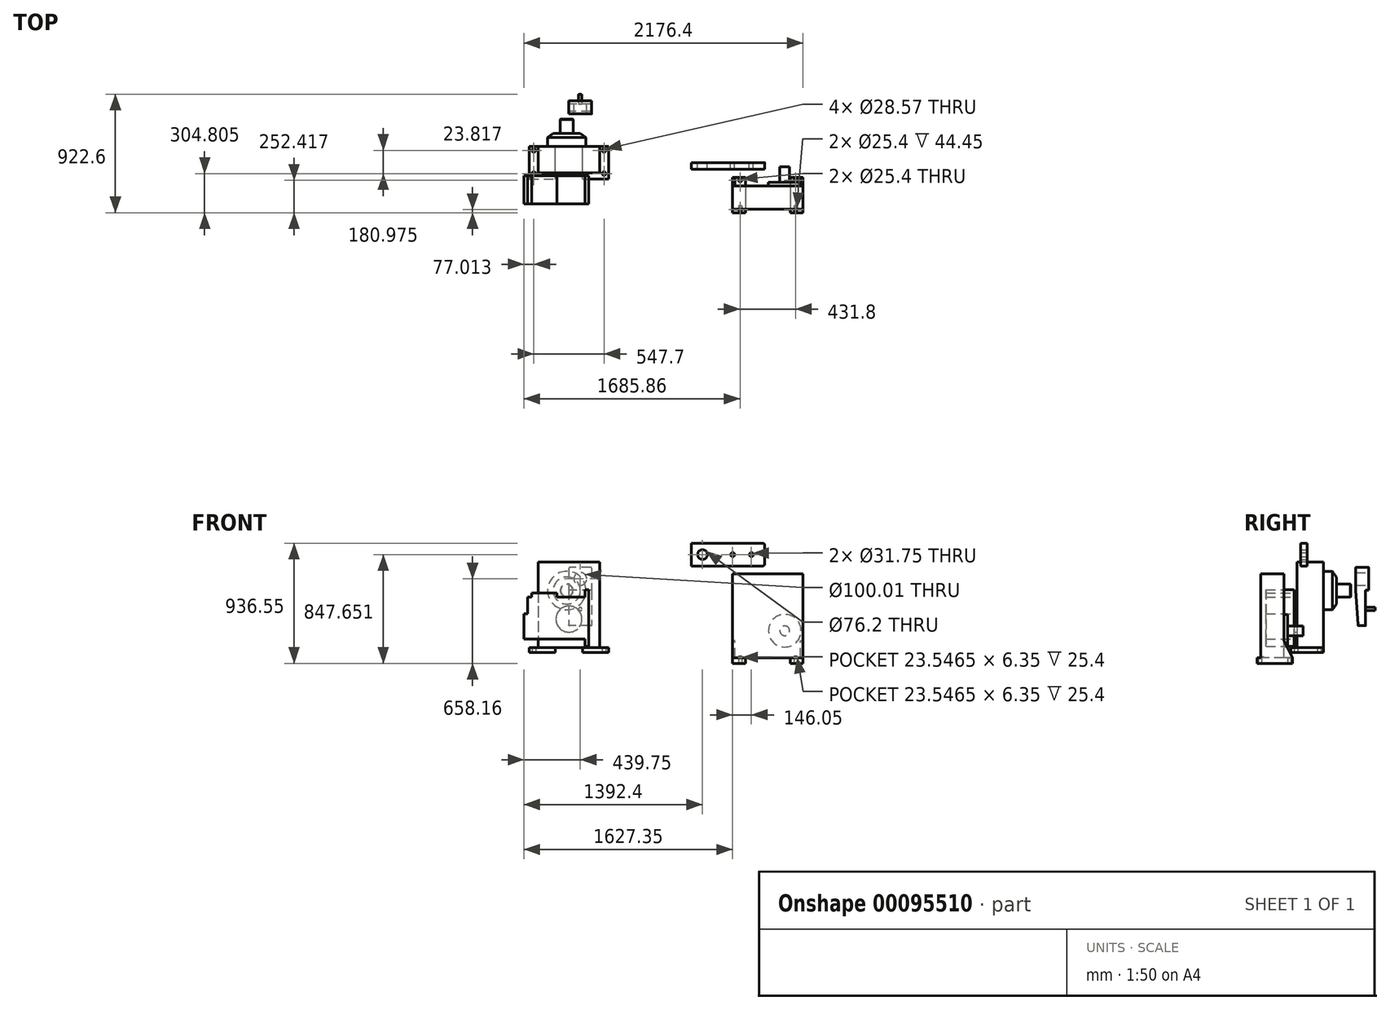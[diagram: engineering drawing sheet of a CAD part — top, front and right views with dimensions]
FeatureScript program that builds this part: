
annotation { "Feature Type Name" : "Feature", "Feature Type Description" : "" }
export const myFeature = defineFeature(function(context is Context, id is Id, definition is map)
    precondition{}
    {
        {
            var Q0;
            Q0=qCreatedBy(makeId("Top.planeOp"),FACE);
            var sketch = newSketch(context, id + "F0", { "sketchPlane" : qUnion([Q0])});
            skLineSegment(sketch, "E0.bottom", {"start": v(-310.36, 127) * mm, "end": v(310.36, 127) * mm});
            skLineSegment(sketch, "E0.top", {"start": v(-310.36, -127) * mm, "end": v(310.36, -127) * mm});
            skLineSegment(sketch, "E0.left", {"start": v(-310.36, 127) * mm, "end": v(-310.36, -127) * mm});
            skLineSegment(sketch, "E0.right", {"start": v(310.36, 127) * mm, "end": v(310.36, -127) * mm});
            skPoint(sketch, "E0.middle", {"position": v(0, 0) * mm});
            skCircle(sketch, "E1", {"center": v(-273.84, -85.73) * mm, "radius": 14.29 * mm});
            skCircle(sketch, "E2.1.0.0", {"center": v(273.86, -85.73) * mm, "radius": 14.29 * mm});
            skLineSegment(sketch, "E2.direction1", {"start": v(-273.84, -85.73) * mm, "end": v(273.86, -85.73) * mm, "construction": true});
            skCircle(sketch, "E3.0.1.0", {"center": v(-273.84, 95.25) * mm, "radius": 14.29 * mm});
            skCircle(sketch, "E3.0.1.1", {"center": v(273.86, 95.25) * mm, "radius": 14.29 * mm});
            skLineSegment(sketch, "E3.direction1", {"start": v(-273.84, -85.73) * mm, "end": v(-248.44, -85.73) * mm, "construction": true});
            skLineSegment(sketch, "E3.direction2", {"start": v(-273.84, -85.73) * mm, "end": v(-273.84, 95.25) * mm, "construction": true});
            skSolve(sketch);
        }
        {
            var Q0;
            Q0=makeQuery(id+"F0.imprint","IMPRINT",FACE,{"disambiguationData":[TD([[makeQuery(id+"F0.imprint","IMPRINT",EDGE,{"derivedFrom":sQuery(id+"F0.wireOp",EDGE,"E0.bottom")}),-1.0]])]});
            extrude(context, id + "F1", {"entities" : qUnion([Q0]), "depth" : 39.7 * mm});
        }
        {
            var Q0;
            Q0=makeQuery(id+"F1.opExtrude","CAP_FACE",FACE,{"disambiguationData":[OSD([sQuery(id+"F0.wireOp",EDGE,"E0.bottom"),sQuery(id+"F0.wireOp",EDGE,"E0.top"),sQuery(id+"F0.wireOp",EDGE,"E0.left"),sQuery(id+"F0.wireOp",EDGE,"E0.right"),sQuery(id+"F0.wireOp",EDGE,"E1"),sQuery(id+"F0.wireOp",EDGE,"E2.1.0.0"),sQuery(id+"F0.wireOp",EDGE,"E3.0.1.0"),sQuery(id+"F0.wireOp",EDGE,"E3.0.1.1")])],"isStart":false});
            var sketch = newSketch(context, id + "F2", { "sketchPlane" : qUnion([Q0])});
            skLineSegment(sketch, "E4.bottom", {"start": v(-240.51, 127) * mm, "end": v(240.51, 127) * mm});
            skLineSegment(sketch, "E4.top", {"start": v(-240.51, -79.37) * mm, "end": v(240.51, -79.37) * mm});
            skLineSegment(sketch, "E4.left", {"start": v(-240.51, 127) * mm, "end": v(-240.51, -79.37) * mm});
            skLineSegment(sketch, "E4.right", {"start": v(240.51, 127) * mm, "end": v(240.51, -79.37) * mm});
            skSolve(sketch);
        }
        {
            var Q0;
            Q0=makeQuery(id+"F2.imprint","IMPRINT",FACE,{"disambiguationData":[TD([[makeQuery(id+"F2.imprint","IMPRINT",EDGE,{"derivedFrom":sQuery(id+"F2.wireOp",EDGE,"E4.bottom")}),-1.0]])]});
            extrude(context, id + "F3", {"entities" : qUnion([Q0]), "operationType" : NewBodyOperationType.ADD, "depth" : 666.75 * mm});
        }
        {
            var Q0;
            Q0=makeQuery(id+"F3.boolean.opBoolean","MERGE",FACE,{"derivedFrom":[makeQuery(id+"F1.opExtrude","SWEPT_FACE",FACE,{"disambiguationData":[OSD([sQuery(id+"F0.wireOp",EDGE,"E0.bottom")])]}),makeQuery(id+"F3.opExtrude","SWEPT_FACE",FACE,{"disambiguationData":[OSD([sQuery(id+"F2.wireOp",EDGE,"E4.bottom")])]})]});
            var sketch = newSketch(context, id + "F4", { "sketchPlane" : qUnion([Q0])});
            skCircle(sketch, "E5", {"center": v(16.66, 483.4) * mm, "radius": 150.02 * mm});
            skSolve(sketch);
        }
        {
            var Q0;
            Q0=makeQuery(id+"F4.imprint","IMPRINT",FACE,{"disambiguationData":[TD([[makeQuery(id+"F4.imprint","IMPRINT",EDGE,{"derivedFrom":sQuery(id+"F4.wireOp",EDGE,"E5")}),1.0]])]});
            extrude(context, id + "F5", {"entities" : qUnion([Q0]), "operationType" : NewBodyOperationType.ADD, "depth" : 101.6 * mm});
        }
        {
            var Q0;
            Q0=makeQuery(id+"F5.opExtrude","CAP_FACE",FACE,{"disambiguationData":[OSD([sQuery(id+"F4.wireOp",EDGE,"E5")])],"isStart":false});
            chamfer(context, id + "F6", {"entities" : qUnion([Q0]), "chamferType" : ChamferType.TWO_OFFSETS, "width1" : 31.75 * mm, "oppositeDirection" : false, "width2" : 44.45 * mm, "tangentPropagation" : true});
        }
        {
            var Q0;
            Q0=qCreatedBy(makeId("Right.planeOp"),FACE);
            var sketch = newSketch(context, id + "F7", { "sketchPlane" : qUnion([Q0])});
            skLineSegment(sketch, "E6.bottom", {"start": v(379.67, 663.04) * mm, "end": v(481.27, 663.04) * mm});
            skLineSegment(sketch, "E7", {"start": v(379.67, 485.24) * mm, "end": v(481.27, 485.24) * mm});
            skLineSegment(sketch, "E8", {"start": v(455.87, 485.24) * mm, "end": v(455.87, 209.02) * mm});
            skLineSegment(sketch, "E9", {"start": v(379.67, 485.24) * mm, "end": v(398.72, 209.02) * mm});
            skLineSegment(sketch, "E10", {"start": v(379.67, 663.04) * mm, "end": v(379.67, 485.24) * mm});
            skLineSegment(sketch, "E11", {"start": v(481.27, 663.04) * mm, "end": v(481.27, 485.24) * mm});
            skLineSegment(sketch, "E12", {"start": v(398.72, 209.02) * mm, "end": v(455.87, 209.02) * mm});
            skSolve(sketch);
        }
        {
            var Q0;
            Q0=makeQuery(id+"F7.imprint","IMPRINT",FACE,{"disambiguationData":[TD([[makeQuery(id+"F7.imprint","IMPRINT",EDGE,{"derivedFrom":sQuery(id+"F7.wireOp",EDGE,"E6.bottom")}),-1.0]])]});
            var Q1;
            {var subQ2=sQuery(id+"F7.wireOp",EDGE,"E8");Q1=makeQuery(id+"F7.imprint","IMPRINT",FACE,{"disambiguationData":[TD([[makeQuery(id+"F7.imprint","IMPRINT",EDGE,{"derivedFrom":subQ2}),-1.0]])]});}
            extrude(context, id + "F8", {"entities" : qUnion([Q0, Q1]), "depth" : 177.8 * mm});
        }
        {
            var Q0;
            Q0=makeQuery(id+"F8.opExtrude","SWEPT_FACE",FACE,{"disambiguationData":[OSD([sQuery(id+"F7.wireOp",EDGE,"E11")])]});
            var sketch = newSketch(context, id + "F9", { "sketchPlane" : qUnion([Q0])});
            skLineSegment(sketch, "E13", {"start": v(-177.8, 485.24) * mm, "end": v(-177.8, 656.7) * mm});
            skLineSegment(sketch, "E14", {"start": v(-171.45, 663.04) * mm, "end": v(0, 663.04) * mm});
            skPoint(sketch, "E15.visualSharp", {"position": v(-177.8, 663.04) * mm});
            skArc(sketch, "E15.filletArc", {"start": v(-171.45, 663.04) * mm, "mid": v(-175.94, 661.18) * mm, "end": v(-177.8, 656.7) * mm});
            skSolve(sketch);
        }
        {
            var Q0;
            {var subQ0=sQuery(id+"F9.wireOp",EDGE,"E15.filletArc");Q0=makeQuery(id+"F9.imprint","IMPRINT",FACE,{"disambiguationData":[TD([[makeQuery(id+"F9.imprint","IMPRINT",EDGE,{"derivedFrom":subQ0}),-1.0]])]});}
            extrude(context, id + "F10", {"entities" : qUnion([Q0]), "operationType" : NewBodyOperationType.REMOVE, "endBound" : BoundingType.UP_TO_NEXT, "oppositeDirection" : true, "depth" : 25.4 * mm});
        }
        {
            var Q0;
            Q0=makeQuery(id+"F8.opExtrude","SWEPT_FACE",FACE,{"disambiguationData":[OSD([sQuery(id+"F7.wireOp",EDGE,"E11")])]});
            var sketch = newSketch(context, id + "F11", { "sketchPlane" : qUnion([Q0])});
            skLineSegment(sketch, "E16", {"start": v(-39.2, 663.04) * mm, "end": v(-6.35, 663.04) * mm});
            skLineSegment(sketch, "E17", {"start": v(0, 656.7) * mm, "end": v(0, 648.47) * mm});
            skPoint(sketch, "E18.visualSharp", {"position": v(0, 663.04) * mm});
            skArc(sketch, "E18.filletArc", {"start": v(0, 656.7) * mm, "mid": v(-1.86, 661.18) * mm, "end": v(-6.35, 663.04) * mm});
            skSolve(sketch);
        }
        {
            var Q0;
            {var subQ0=sQuery(id+"F11.wireOp",EDGE,"E18.filletArc");Q0=makeQuery(id+"F11.imprint","IMPRINT",FACE,{"disambiguationData":[TD([[makeQuery(id+"F11.imprint","IMPRINT",EDGE,{"derivedFrom":subQ0}),-1.0]])]});}
            extrude(context, id + "F12", {"entities" : qUnion([Q0]), "operationType" : NewBodyOperationType.REMOVE, "endBound" : BoundingType.UP_TO_NEXT, "oppositeDirection" : true, "depth" : 25.4 * mm});
        }
        {
            var Q0;
            Q0=makeQuery(id+"F8.opExtrude","SWEPT_FACE",FACE,{"disambiguationData":[OSD([sQuery(id+"F7.wireOp",EDGE,"E8")])]});
            var sketch = newSketch(context, id + "F13", { "sketchPlane" : qUnion([Q0])});
            skLineSegment(sketch, "E19", {"start": v(-177.8, 248.8) * mm, "end": v(-177.8, 215.37) * mm});
            skLineSegment(sketch, "E20", {"start": v(-171.45, 209.02) * mm, "end": v(-6.35, 209.02) * mm});
            skLineSegment(sketch, "E21", {"start": v(0, 215.37) * mm, "end": v(0, 249.23) * mm});
            skPoint(sketch, "E22.visualSharp", {"position": v(-177.8, 209.02) * mm});
            skArc(sketch, "E22.filletArc", {"start": v(-177.8, 215.37) * mm, "mid": v(-175.94, 210.88) * mm, "end": v(-171.45, 209.02) * mm});
            skPoint(sketch, "E23.visualSharp", {"position": v(0, 209.02) * mm});
            skArc(sketch, "E23.filletArc", {"start": v(-6.35, 209.02) * mm, "mid": v(-1.86, 210.88) * mm, "end": v(0, 215.37) * mm});
            skSolve(sketch);
        }
        {
            var Q0;
            {var subQ0=sQuery(id+"F13.wireOp",EDGE,"E22.filletArc");Q0=makeQuery(id+"F13.imprint","IMPRINT",FACE,{"disambiguationData":[TD([[makeQuery(id+"F13.imprint","IMPRINT",EDGE,{"derivedFrom":subQ0}),-1.0]])]});}
            extrude(context, id + "F14", {"entities" : qUnion([Q0]), "operationType" : NewBodyOperationType.REMOVE, "endBound" : BoundingType.UP_TO_NEXT, "oppositeDirection" : true, "depth" : 25.4 * mm});
        }
        {
            var Q0;
            {var subQ0=sQuery(id+"F13.wireOp",EDGE,"E23.filletArc");Q0=makeQuery(id+"F13.imprint","IMPRINT",FACE,{"disambiguationData":[TD([[makeQuery(id+"F13.imprint","IMPRINT",EDGE,{"derivedFrom":subQ0}),-1.0]])]});}
            extrude(context, id + "F15", {"entities" : qUnion([Q0]), "operationType" : NewBodyOperationType.REMOVE, "endBound" : BoundingType.UP_TO_NEXT, "oppositeDirection" : true, "depth" : 25.4 * mm});
        }
        {
            var Q0;
            Q0=makeQuery(id+"F8.opExtrude","SWEPT_FACE",FACE,{"disambiguationData":[OSD([sQuery(id+"F7.wireOp",EDGE,"E11")])]});
            var sketch = newSketch(context, id + "F16", { "sketchPlane" : qUnion([Q0])});
            skCircle(sketch, "E24", {"center": v(-88.9, 574.14) * mm, "radius": 50 * mm});
            skSolve(sketch);
        }
        {
            var Q0;
            Q0=makeQuery(id+"F16.imprint","IMPRINT",FACE,{"disambiguationData":[TD([[makeQuery(id+"F16.imprint","IMPRINT",EDGE,{"derivedFrom":sQuery(id+"F16.wireOp",EDGE,"E24")}),1.0]])]});
            extrude(context, id + "F17", {"entities" : qUnion([Q0]), "operationType" : NewBodyOperationType.REMOVE, "endBound" : BoundingType.UP_TO_NEXT, "oppositeDirection" : true, "depth" : 25.4 * mm});
        }
        {
            var Q0;
            Q0=makeQuery(id+"F3.boolean.opBoolean","MERGE",FACE,{"derivedFrom":[makeQuery(id+"F1.opExtrude","SWEPT_FACE",FACE,{"disambiguationData":[OSD([sQuery(id+"F0.wireOp",EDGE,"E0.bottom")])]}),makeQuery(id+"F3.opExtrude","SWEPT_FACE",FACE,{"disambiguationData":[OSD([sQuery(id+"F2.wireOp",EDGE,"E4.bottom")])]})]});
            var sketch = newSketch(context, id + "F18", { "sketchPlane" : qUnion([Q0])});
            skLineSegment(sketch, "E25", {"start": v(-240.51, 39.7) * mm, "end": v(240.51, 39.7) * mm});
            skLineSegment(sketch, "E26.bottom", {"start": v(-106.37, 0) * mm, "end": v(106.36, 0) * mm});
            skLineSegment(sketch, "E26.top", {"start": v(-106.37, 39.7) * mm, "end": v(106.36, 39.7) * mm});
            skLineSegment(sketch, "E26.left", {"start": v(-106.37, 0) * mm, "end": v(-106.37, 39.7) * mm});
            skLineSegment(sketch, "E26.right", {"start": v(106.36, 0) * mm, "end": v(106.36, 39.7) * mm});
            skSolve(sketch);
        }
        {
            var Q0;
            Q0=makeQuery(id+"F18.imprint","IMPRINT",FACE,{"disambiguationData":[TD([[makeQuery(id+"F18.imprint","IMPRINT",EDGE,{"derivedFrom":sQuery(id+"F18.wireOp",EDGE,"E26.bottom")}),-1.0]])]});
            extrude(context, id + "F19", {"entities" : qUnion([Q0]), "operationType" : NewBodyOperationType.REMOVE, "endBound" : BoundingType.UP_TO_NEXT, "oppositeDirection" : true, "depth" : 25.4 * mm});
        }
        {
            var Q0;
            Q0=makeQuery(id+"F5.opExtrude","CAP_FACE",FACE,{"disambiguationData":[OSD([sQuery(id+"F4.wireOp",EDGE,"E5")])],"isStart":false});
            var sketch = newSketch(context, id + "F20", { "sketchPlane" : qUnion([Q0])});
            skCircle(sketch, "E27", {"center": v(16.66, 483.4) * mm, "radius": 50 * mm});
            skSolve(sketch);
        }
        {
            var Q0;
            Q0=makeQuery(id+"F20.imprint","IMPRINT",FACE,{"disambiguationData":[TD([[makeQuery(id+"F20.imprint","IMPRINT",EDGE,{"derivedFrom":sQuery(id+"F20.wireOp",EDGE,"E27")}),1.0]])]});
            extrude(context, id + "F21", {"entities" : qUnion([Q0]), "operationType" : NewBodyOperationType.ADD, "depth" : 111.12 * mm});
        }
        {
            var Q0;
            Q0=makeQuery(id+"F21.opExtrude","CAP_EDGE",EDGE,{"disambiguationData":[OSD([sQuery(id+"F20.wireOp",EDGE,"E27")])],"isStart":false});
            chamfer(context, id + "F22", {"entities" : qUnion([Q0]), "width" : 3.17 * mm, "tangentPropagation" : true});
        }
        {
            var Q0;
            Q0=makeQuery(id+"F8.opExtrude","SWEPT_FACE",FACE,{"disambiguationData":[OSD([sQuery(id+"F7.wireOp",EDGE,"E8")])]});
            var sketch = newSketch(context, id + "F23", { "sketchPlane" : qUnion([Q0])});
            skCircle(sketch, "E28", {"center": v(-88.9, 339.2) * mm, "radius": 12.7 * mm});
            skPoint(sketch, "E28.centerSnap0", {"position": v(-88.9, 209.02) * mm});
            skSolve(sketch);
        }
        {
            var Q0;
            Q0=makeQuery(id+"F23.imprint","IMPRINT",FACE,{"disambiguationData":[TD([[makeQuery(id+"F23.imprint","IMPRINT",EDGE,{"derivedFrom":sQuery(id+"F23.wireOp",EDGE,"E28")}),1.0]])]});
            extrude(context, id + "F24", {"entities" : qUnion([Q0]), "operationType" : NewBodyOperationType.ADD, "depth" : 76.2 * mm});
        }
        {
            var Q0;
            Q0=qCreatedBy(makeId("Front.planeOp"),FACE);
            var sketch = newSketch(context, id + "F25", { "sketchPlane" : qUnion([Q0])});
            skLineSegment(sketch, "E29.bottom", {"start": v(723.82, 612.89) * mm, "end": v(1274.68, 612.89) * mm});
            skLineSegment(sketch, "E29.top", {"start": v(723.82, -84.02) * mm, "end": v(1274.68, -84.02) * mm});
            skLineSegment(sketch, "E29.left", {"start": v(723.82, 612.89) * mm, "end": v(723.82, -84.02) * mm});
            skLineSegment(sketch, "E29.right", {"start": v(1274.68, 612.89) * mm, "end": v(1274.68, -84.02) * mm});
            skLineSegment(sketch, "E30", {"start": v(824.63, -84.02) * mm, "end": v(824.63, -39.57) * mm});
            skLineSegment(sketch, "E31", {"start": v(824.63, -39.57) * mm, "end": v(1173.88, -39.57) * mm});
            skLineSegment(sketch, "E32", {"start": v(1173.88, -39.57) * mm, "end": v(1173.88, -84.02) * mm});
            skCircle(sketch, "E33", {"center": v(866.7, 169.98) * mm, "radius": 127 * mm});
            skLineSegment(sketch, "E34", {"start": v(1173.88, -39.57) * mm, "end": v(1255.63, -39.57) * mm});
            skLineSegment(sketch, "E35", {"start": v(1255.63, -39.57) * mm, "end": v(1255.63, 93.78) * mm});
            skLineSegment(sketch, "E36", {"start": v(1255.63, 93.78) * mm, "end": v(1274.68, 93.78) * mm});
            skLineSegment(sketch, "E37", {"start": v(824.63, -39.57) * mm, "end": v(742.87, -39.57) * mm});
            skLineSegment(sketch, "E38", {"start": v(742.87, -39.57) * mm, "end": v(742.87, 93.78) * mm});
            skLineSegment(sketch, "E39", {"start": v(742.87, 93.78) * mm, "end": v(723.82, 93.78) * mm});
            skLineSegment(sketch, "E40", {"start": v(1255.63, 93.78) * mm, "end": v(618.06, 93.78) * mm, "construction": true});
            skCircle(sketch, "E41", {"center": v(866.7, 169.98) * mm, "radius": 38.1 * mm});
            skSolve(sketch);
        }
        {
            var Q0;
            Q0=makeQuery(id+"F25.imprint","IMPRINT",FACE,{"disambiguationData":[TD([[makeQuery(id+"F25.imprint","IMPRINT",EDGE,{"derivedFrom":sQuery(id+"F25.wireOp",EDGE,"E33")}),1.0]])]});
            extrude(context, id + "F26", {"entities" : qUnion([Q0]), "depth" : 209.55 * mm});
        }
        {
            var Q0;
            Q0=makeQuery(id+"F25.imprint","IMPRINT",FACE,{"disambiguationData":[TD([[makeQuery(id+"F25.imprint","IMPRINT",EDGE,{"derivedFrom":sQuery(id+"F25.wireOp",EDGE,"E29.bottom")}),-1.0]])]});
            extrude(context, id + "F27", {"entities" : qUnion([Q0]), "operationType" : NewBodyOperationType.ADD, "depth" : 180.97 * mm});
        }
        {
            var Q0;
            {var subQ4=sQuery(id+"F25.wireOp",EDGE,"E32");Q0=makeQuery(id+"F25.imprint","IMPRINT",FACE,{"disambiguationData":[TD([[makeQuery(id+"F25.imprint","IMPRINT",EDGE,{"derivedFrom":subQ4}),1.0]])]});}
            var Q1;
            {var subQ4=sQuery(id+"F25.wireOp",EDGE,"E30");Q1=makeQuery(id+"F25.imprint","IMPRINT",FACE,{"disambiguationData":[TD([[makeQuery(id+"F25.imprint","IMPRINT",EDGE,{"derivedFrom":subQ4}),1.0]])]});}
            extrude(context, id + "F28", {"entities" : qUnion([Q0, Q1]), "operationType" : NewBodyOperationType.ADD, "depth" : 247.65 * mm});
        }
        {
            var Q0;
            {var subQ0=sQuery(id+"F25.wireOp",EDGE,"E29.right");Q0=makeQuery(id+"F28.boolean.opBoolean","MERGE",FACE,{"derivedFrom":[makeQuery(id+"F27.opExtrude","SWEPT_FACE",FACE,{"disambiguationData":[OSD([subQ0])]}),makeQuery(id+"F28.opExtrude","SWEPT_FACE",FACE,{"disambiguationData":[OSD([subQ0])]})]});}
            var sketch = newSketch(context, id + "F29", { "sketchPlane" : qUnion([Q0])});
            skPoint(sketch, "E42.0", {"position": v(-247.65, -39.57) * mm});
            skLineSegment(sketch, "E43", {"start": v(-180.97, 93.78) * mm, "end": v(-247.65, -39.57) * mm});
            skSolve(sketch);
        }
        {
            var Q0;
            {var subQ0=sQuery(id+"F29.wireOp",EDGE,"E43");Q0=makeQuery(id+"F29.imprint","IMPRINT",FACE,{"disambiguationData":[TD([[makeQuery(id+"F29.imprint","IMPRINT",EDGE,{"derivedFrom":subQ0}),-1.0]])]});}
            extrude(context, id + "F30", {"entities" : qUnion([Q0]), "operationType" : NewBodyOperationType.REMOVE, "endBound" : BoundingType.UP_TO_NEXT, "oppositeDirection" : true, "depth" : 25.4 * mm});
        }
        {
            var Q0;
            {var subQ0=sQuery(id+"F25.wireOp",EDGE,"E29.left");Q0=makeQuery(id+"F28.boolean.opBoolean","MERGE",FACE,{"derivedFrom":[makeQuery(id+"F27.opExtrude","SWEPT_FACE",FACE,{"disambiguationData":[OSD([subQ0])]}),makeQuery(id+"F28.opExtrude","SWEPT_FACE",FACE,{"disambiguationData":[OSD([subQ0])]})]});}
            var sketch = newSketch(context, id + "F31", { "sketchPlane" : qUnion([Q0])});
            skPoint(sketch, "E44.0", {"position": v(247.65, -39.57) * mm});
            skLineSegment(sketch, "E45", {"start": v(180.97, 93.78) * mm, "end": v(247.65, -39.57) * mm});
            skSolve(sketch);
        }
        {
            var Q0;
            {var subQ0=sQuery(id+"F31.wireOp",EDGE,"E45");Q0=makeQuery(id+"F31.imprint","IMPRINT",FACE,{"disambiguationData":[TD([[makeQuery(id+"F31.imprint","IMPRINT",EDGE,{"derivedFrom":subQ0}),1.0]])]});}
            extrude(context, id + "F32", {"entities" : qUnion([Q0]), "operationType" : NewBodyOperationType.REMOVE, "endBound" : BoundingType.UP_TO_NEXT, "oppositeDirection" : true, "depth" : 25.4 * mm});
        }
        {
            var Q0;
            {var subQ0=sQuery(id+"F25.wireOp",EDGE,"E36");var subQ1=sQuery(id+"F25.wireOp",EDGE,"E35");var subQ2=sQuery(id+"F25.wireOp",EDGE,"E34");var subQ3=sQuery(id+"F25.wireOp",EDGE,"E29.right");var subQ4=sQuery(id+"F25.wireOp",EDGE,"E29.top");var subQ5=sQuery(id+"F25.wireOp",EDGE,"E39");var subQ6=sQuery(id+"F25.wireOp",EDGE,"E38");var subQ7=sQuery(id+"F25.wireOp",EDGE,"E37");var subQ8=sQuery(id+"F25.wireOp",EDGE,"E29.left");var subQ9=sQuery(id+"F25.wireOp",EDGE,"E33");Q0=makeQuery(id+"F28.boolean.opBoolean","MERGE",FACE,{"derivedFrom":[makeQuery(id+"F27.boolean.opBoolean","MERGE",FACE,{"derivedFrom":[makeQuery(id+"F26.opExtrude","CAP_FACE",FACE,{"disambiguationData":[OSD([subQ9])],"isStart":true}),makeQuery(id+"F27.opExtrude","CAP_FACE",FACE,{"disambiguationData":[OSD([sQuery(id+"F25.wireOp",EDGE,"E29.bottom"),subQ8,subQ3,sQuery(id+"F25.wireOp",EDGE,"E31"),subQ9,subQ2,subQ1,subQ0,subQ7,subQ6,subQ5])],"isStart":true})]}),makeQuery(id+"F28.opExtrude","CAP_FACE",FACE,{"disambiguationData":[OSD([subQ4,subQ8,sQuery(id+"F25.wireOp",EDGE,"E30"),subQ7,subQ6,subQ5])],"isStart":true}),makeQuery(id+"F28.opExtrude","CAP_FACE",FACE,{"disambiguationData":[OSD([subQ4,subQ3,sQuery(id+"F25.wireOp",EDGE,"E32"),subQ2,subQ1,subQ0])],"isStart":true})]});}
            var sketch = newSketch(context, id + "F33", { "sketchPlane" : qUnion([Q0])});
            skLineSegment(sketch, "E46", {"start": v(-1173.88, -39.57) * mm, "end": v(-1274.68, -39.57) * mm});
            skSolve(sketch);
        }
        {
            var Q0;
            {var subQ0=sQuery(id+"F33.wireOp",EDGE,"E46");Q0=makeQuery(id+"F33.imprint","IMPRINT",FACE,{"disambiguationData":[TD([[makeQuery(id+"F33.imprint","IMPRINT",EDGE,{"derivedFrom":subQ0}),1.0]])]});}
            extrude(context, id + "F34", {"entities" : qUnion([Q0]), "operationType" : NewBodyOperationType.ADD, "depth" : 28.57 * mm});
        }
        {
            var Q0;
            {var subQ0=sQuery(id+"F25.wireOp",EDGE,"E36");var subQ1=sQuery(id+"F25.wireOp",EDGE,"E35");var subQ2=sQuery(id+"F25.wireOp",EDGE,"E34");var subQ3=sQuery(id+"F25.wireOp",EDGE,"E29.right");var subQ4=sQuery(id+"F25.wireOp",EDGE,"E29.top");var subQ5=sQuery(id+"F25.wireOp",EDGE,"E39");var subQ6=sQuery(id+"F25.wireOp",EDGE,"E38");var subQ7=sQuery(id+"F25.wireOp",EDGE,"E37");var subQ8=sQuery(id+"F25.wireOp",EDGE,"E29.left");var subQ9=sQuery(id+"F25.wireOp",EDGE,"E33");Q0=makeQuery(id+"F28.boolean.opBoolean","MERGE",FACE,{"derivedFrom":[makeQuery(id+"F27.boolean.opBoolean","MERGE",FACE,{"derivedFrom":[makeQuery(id+"F26.opExtrude","CAP_FACE",FACE,{"disambiguationData":[OSD([subQ9])],"isStart":true}),makeQuery(id+"F27.opExtrude","CAP_FACE",FACE,{"disambiguationData":[OSD([sQuery(id+"F25.wireOp",EDGE,"E29.bottom"),subQ8,subQ3,sQuery(id+"F25.wireOp",EDGE,"E31"),subQ9,subQ2,subQ1,subQ0,subQ7,subQ6,subQ5])],"isStart":true})]}),makeQuery(id+"F28.opExtrude","CAP_FACE",FACE,{"disambiguationData":[OSD([subQ4,subQ8,sQuery(id+"F25.wireOp",EDGE,"E30"),subQ7,subQ6,subQ5])],"isStart":true}),makeQuery(id+"F28.opExtrude","CAP_FACE",FACE,{"disambiguationData":[OSD([subQ4,subQ3,sQuery(id+"F25.wireOp",EDGE,"E32"),subQ2,subQ1,subQ0])],"isStart":true})]});}
            var sketch = newSketch(context, id + "F35", { "sketchPlane" : qUnion([Q0])});
            skLineSegment(sketch, "E47", {"start": v(-824.63, -39.57) * mm, "end": v(-723.82, -39.57) * mm});
            skSolve(sketch);
        }
        {
            var Q0;
            Q0 = qSketchRegion(id + "F35", true);
            var Q1;
            {var subQ0=sQuery(id+"F35.wireOp",EDGE,"E47");Q1=makeQuery(id+"F35.imprint","IMPRINT",FACE,{"disambiguationData":[TD([[makeQuery(id+"F35.imprint","IMPRINT",EDGE,{"derivedFrom":subQ0}),-1.0]])]});}
            extrude(context, id + "F36", {"entities" : qUnion([Q0, Q1]), "operationType" : NewBodyOperationType.ADD, "depth" : 28.57 * mm});
        }
        {
            var Q0;
            Q0=qCreatedBy(makeId("Front.planeOp"),FACE);
            var sketch = newSketch(context, id + "F37", { "sketchPlane" : qUnion([Q0])});
            skLineSegment(sketch, "E48.bottom", {"start": v(955.82, 852.53) * mm, "end": v(1508.27, 852.53) * mm});
            skLineSegment(sketch, "E48.top", {"start": v(955.82, 674.73) * mm, "end": v(1508.27, 674.73) * mm});
            skLineSegment(sketch, "E48.left", {"start": v(955.82, 852.53) * mm, "end": v(955.82, 674.73) * mm});
            skLineSegment(sketch, "E48.right", {"start": v(1527.32, 833.48) * mm, "end": v(1527.32, 693.78) * mm});
            skCircle(sketch, "E49", {"center": v(1041.55, 763.63) * mm, "radius": 38.1 * mm});
            skPoint(sketch, "E49.centerSnap0", {"position": v(955.82, 763.63) * mm});
            skPoint(sketch, "E50.visualSharp", {"position": v(1527.32, 852.53) * mm});
            skArc(sketch, "E50.filletArc", {"start": v(1527.32, 833.48) * mm, "mid": v(1521.74, 846.95) * mm, "end": v(1508.27, 852.53) * mm});
            skPoint(sketch, "E51.visualSharp", {"position": v(1527.32, 674.73) * mm});
            skArc(sketch, "E51.filletArc", {"start": v(1508.27, 674.73) * mm, "mid": v(1521.74, 680.31) * mm, "end": v(1527.32, 693.78) * mm});
            skCircle(sketch, "E52", {"center": v(1422.55, 763.63) * mm, "radius": 15.88 * mm});
            skCircle(sketch, "E53", {"center": v(1276.5, 763.63) * mm, "radius": 15.88 * mm});
            skSolve(sketch);
        }
        {
            var Q0;
            Q0=makeQuery(id+"F37.imprint","IMPRINT",FACE,{"disambiguationData":[TD([[makeQuery(id+"F37.imprint","IMPRINT",EDGE,{"derivedFrom":sQuery(id+"F37.wireOp",EDGE,"E48.bottom")}),-1.0]])]});
            extrude(context, id + "F38", {"entities" : qUnion([Q0]), "depth" : 50.8 * mm});
        }
        {
            var Q0;
            Q0=makeQuery(id+"F25.imprint","IMPRINT",FACE,{"disambiguationData":[TD([[makeQuery(id+"F25.imprint","IMPRINT",EDGE,{"derivedFrom":sQuery(id+"F25.wireOp",EDGE,"E41")}),1.0]])]});
            extrude(context, id + "F39", {"entities" : qUnion([Q0]), "operationType" : NewBodyOperationType.ADD, "depth" : 330.2 * mm});
        }
        {
            var Q0;
            {var subQ0=sQuery(id+"F25.wireOp",EDGE,"E29.top");Q0=makeQuery(id+"F34.boolean.opBoolean","MERGE",FACE,{"derivedFrom":[makeQuery(id+"F28.opExtrude","SWEPT_FACE",FACE,{"disambiguationData":[OSD([subQ0]),TDD([makeQuery(id+"F25.imprint","IMPRINT",EDGE,{"disambiguationData":[TD([[makeQuery(id+"F25.imprint","INTERSECT",VERTEX,{"derivedFrom":[subQ0,sQuery(id+"F25.wireOp",EDGE,"E29.right")]}),1.0]])],"derivedFrom":subQ0})])]}),makeQuery(id+"F34.opExtrude","SWEPT_FACE",FACE,{"disambiguationData":[OSD([subQ0])]})]});}
            var sketch = newSketch(context, id + "F40", { "sketchPlane" : qUnion([Q0])});
            skPoint(sketch, "E54.0", {"position": v(723.82, 247.65) * mm});
            skCircle(sketch, "E55", {"center": v(782.56, 223.84) * mm, "radius": 12.7 * mm});
            skCircle(sketch, "E56.0.1.0", {"center": v(782.56, -4.76) * mm, "radius": 12.7 * mm});
            skCircle(sketch, "E56.1.0.0", {"center": v(1214.36, 223.84) * mm, "radius": 12.7 * mm});
            skCircle(sketch, "E56.1.1.0", {"center": v(1214.36, -4.76) * mm, "radius": 12.7 * mm});
            skLineSegment(sketch, "E56.direction1", {"start": v(782.56, 223.84) * mm, "end": v(1214.36, 223.84) * mm, "construction": true});
            skLineSegment(sketch, "E56.direction2", {"start": v(782.56, 223.84) * mm, "end": v(782.56, -4.76) * mm, "construction": true});
            skSolve(sketch);
        }
        {
            var Q0;
            Q0=makeQuery(id+"F40.imprint","IMPRINT",FACE,{"disambiguationData":[TD([[makeQuery(id+"F40.imprint","IMPRINT",EDGE,{"derivedFrom":sQuery(id+"F40.wireOp",EDGE,"E55")}),1.0]])]});
            var Q1;
            Q1=makeQuery(id+"F40.imprint","IMPRINT",FACE,{"disambiguationData":[TD([[makeQuery(id+"F40.imprint","IMPRINT",EDGE,{"derivedFrom":sQuery(id+"F40.wireOp",EDGE,"E56.0.1.0")}),1.0]])]});
            var Q2;
            Q2=makeQuery(id+"F40.imprint","IMPRINT",FACE,{"disambiguationData":[TD([[makeQuery(id+"F40.imprint","IMPRINT",EDGE,{"derivedFrom":sQuery(id+"F40.wireOp",EDGE,"E56.1.1.0")}),1.0]])]});
            var Q3;
            Q3=makeQuery(id+"F40.imprint","IMPRINT",FACE,{"disambiguationData":[TD([[makeQuery(id+"F40.imprint","IMPRINT",EDGE,{"derivedFrom":sQuery(id+"F40.wireOp",EDGE,"E56.1.0.0")}),1.0]])]});
            extrude(context, id + "F41", {"entities" : qUnion([Q0, Q1, Q2, Q3]), "operationType" : NewBodyOperationType.REMOVE, "oppositeDirection" : true, "depth" : 50.8 * mm});
        }
        {
            var Q0;
            {var subQ0=sQuery(id+"F25.wireOp",EDGE,"E41");var subQ1=sQuery(id+"F25.wireOp",EDGE,"E36");var subQ2=sQuery(id+"F25.wireOp",EDGE,"E35");var subQ3=sQuery(id+"F25.wireOp",EDGE,"E34");var subQ4=sQuery(id+"F25.wireOp",EDGE,"E29.right");var subQ5=sQuery(id+"F25.wireOp",EDGE,"E29.top");var subQ6=sQuery(id+"F25.wireOp",EDGE,"E39");var subQ7=sQuery(id+"F25.wireOp",EDGE,"E38");var subQ8=sQuery(id+"F25.wireOp",EDGE,"E37");var subQ9=sQuery(id+"F25.wireOp",EDGE,"E29.left");var subQ10=sQuery(id+"F25.wireOp",EDGE,"E33");Q0=makeQuery(id+"F39.boolean.opBoolean","MERGE",FACE,{"derivedFrom":[makeQuery(id+"F28.boolean.opBoolean","MERGE",FACE,{"derivedFrom":[makeQuery(id+"F27.boolean.opBoolean","MERGE",FACE,{"derivedFrom":[makeQuery(id+"F26.opExtrude","CAP_FACE",FACE,{"disambiguationData":[OSD([subQ10,subQ0])],"isStart":true}),makeQuery(id+"F27.opExtrude","CAP_FACE",FACE,{"disambiguationData":[OSD([sQuery(id+"F25.wireOp",EDGE,"E29.bottom"),subQ9,subQ4,sQuery(id+"F25.wireOp",EDGE,"E31"),subQ10,subQ3,subQ2,subQ1,subQ8,subQ7,subQ6])],"isStart":true})]}),makeQuery(id+"F28.opExtrude","CAP_FACE",FACE,{"disambiguationData":[OSD([subQ5,subQ9,sQuery(id+"F25.wireOp",EDGE,"E30"),subQ8,subQ7,subQ6])],"isStart":true}),makeQuery(id+"F28.opExtrude","CAP_FACE",FACE,{"disambiguationData":[OSD([subQ5,subQ4,sQuery(id+"F25.wireOp",EDGE,"E32"),subQ3,subQ2,subQ1])],"isStart":true})]}),makeQuery(id+"F39.opExtrude","CAP_FACE",FACE,{"disambiguationData":[OSD([subQ0])],"isStart":true})]});}
            var sketch = newSketch(context, id + "F42", { "sketchPlane" : qUnion([Q0])});
            skLineSegment(sketch, "E57.bottom", {"start": v(-1274.68, -39.57) * mm, "end": v(-1147.68, -39.57) * mm});
            skLineSegment(sketch, "E57.top", {"start": v(-1274.68, 163.63) * mm, "end": v(-1147.68, 163.63) * mm});
            skLineSegment(sketch, "E57.left", {"start": v(-1274.68, -39.57) * mm, "end": v(-1274.68, 163.63) * mm});
            skLineSegment(sketch, "E57.right", {"start": v(-1147.68, -39.57) * mm, "end": v(-1147.68, 163.63) * mm});
            skLineSegment(sketch, "E58.bottom", {"start": v(-723.82, -39.57) * mm, "end": v(-850.82, -39.57) * mm});
            skLineSegment(sketch, "E58.top", {"start": v(-723.82, 163.63) * mm, "end": v(-850.82, 163.63) * mm});
            skLineSegment(sketch, "E58.left", {"start": v(-723.82, -39.57) * mm, "end": v(-723.82, 163.63) * mm});
            skLineSegment(sketch, "E58.right", {"start": v(-850.82, -39.57) * mm, "end": v(-850.82, 163.63) * mm});
            skSolve(sketch);
        }
        {
            var Q0;
            {var subQ1=sQuery(id+"F40.wireOp",EDGE,"E56.1.1.0");var subQ3=sQuery(id+"F25.wireOp",EDGE,"E41");var subQ4=sQuery(id+"F25.wireOp",EDGE,"E36");var subQ5=sQuery(id+"F25.wireOp",EDGE,"E35");var subQ6=sQuery(id+"F25.wireOp",EDGE,"E34");var subQ7=sQuery(id+"F25.wireOp",EDGE,"E29.right");var subQ8=sQuery(id+"F25.wireOp",EDGE,"E29.top");var subQ9=sQuery(id+"F25.wireOp",EDGE,"E39");var subQ10=sQuery(id+"F25.wireOp",EDGE,"E38");var subQ11=sQuery(id+"F25.wireOp",EDGE,"E37");var subQ12=sQuery(id+"F25.wireOp",EDGE,"E29.left");var subQ13=sQuery(id+"F25.wireOp",EDGE,"E33");var subQ14=makeQuery(id+"F39.boolean.opBoolean","MERGE",FACE,{"derivedFrom":[makeQuery(id+"F28.boolean.opBoolean","MERGE",FACE,{"derivedFrom":[makeQuery(id+"F27.boolean.opBoolean","MERGE",FACE,{"derivedFrom":[makeQuery(id+"F26.opExtrude","CAP_FACE",FACE,{"disambiguationData":[OSD([subQ13,subQ3])],"isStart":true}),makeQuery(id+"F27.opExtrude","CAP_FACE",FACE,{"disambiguationData":[OSD([sQuery(id+"F25.wireOp",EDGE,"E29.bottom"),subQ12,subQ7,sQuery(id+"F25.wireOp",EDGE,"E31"),subQ13,subQ6,subQ5,subQ4,subQ11,subQ10,subQ9])],"isStart":true})]}),makeQuery(id+"F28.opExtrude","CAP_FACE",FACE,{"disambiguationData":[OSD([subQ8,subQ12,sQuery(id+"F25.wireOp",EDGE,"E30"),subQ11,subQ10,subQ9])],"isStart":true}),makeQuery(id+"F28.opExtrude","CAP_FACE",FACE,{"disambiguationData":[OSD([subQ8,subQ7,sQuery(id+"F25.wireOp",EDGE,"E32"),subQ6,subQ5,subQ4])],"isStart":true})]}),makeQuery(id+"F39.opExtrude","CAP_FACE",FACE,{"disambiguationData":[OSD([subQ3])],"isStart":true})]});Q0=makeQuery(id+"F42.imprint","IMPRINT",FACE,{"disambiguationData":[TD([[makeQuery(id+"F42.imprint","IMPRINT",EDGE,{"derivedFrom":makeQuery(id+"F41.boolean.opBoolean","INTERSECT",EDGE,{"derivedFrom":[subQ14,makeQuery(id+"F41.opExtrude","CAP_FACE",FACE,{"disambiguationData":[OSD([subQ1])],"isStart":false})]})}),1.0]])]});}
            var Q1;
            {var subQ1=sQuery(id+"F40.wireOp",EDGE,"E56.0.1.0");var subQ3=sQuery(id+"F25.wireOp",EDGE,"E41");var subQ4=sQuery(id+"F25.wireOp",EDGE,"E36");var subQ5=sQuery(id+"F25.wireOp",EDGE,"E35");var subQ6=sQuery(id+"F25.wireOp",EDGE,"E34");var subQ7=sQuery(id+"F25.wireOp",EDGE,"E29.right");var subQ8=sQuery(id+"F25.wireOp",EDGE,"E29.top");var subQ9=sQuery(id+"F25.wireOp",EDGE,"E39");var subQ10=sQuery(id+"F25.wireOp",EDGE,"E38");var subQ11=sQuery(id+"F25.wireOp",EDGE,"E37");var subQ12=sQuery(id+"F25.wireOp",EDGE,"E29.left");var subQ13=sQuery(id+"F25.wireOp",EDGE,"E33");var subQ14=makeQuery(id+"F39.boolean.opBoolean","MERGE",FACE,{"derivedFrom":[makeQuery(id+"F28.boolean.opBoolean","MERGE",FACE,{"derivedFrom":[makeQuery(id+"F27.boolean.opBoolean","MERGE",FACE,{"derivedFrom":[makeQuery(id+"F26.opExtrude","CAP_FACE",FACE,{"disambiguationData":[OSD([subQ13,subQ3])],"isStart":true}),makeQuery(id+"F27.opExtrude","CAP_FACE",FACE,{"disambiguationData":[OSD([sQuery(id+"F25.wireOp",EDGE,"E29.bottom"),subQ12,subQ7,sQuery(id+"F25.wireOp",EDGE,"E31"),subQ13,subQ6,subQ5,subQ4,subQ11,subQ10,subQ9])],"isStart":true})]}),makeQuery(id+"F28.opExtrude","CAP_FACE",FACE,{"disambiguationData":[OSD([subQ8,subQ12,sQuery(id+"F25.wireOp",EDGE,"E30"),subQ11,subQ10,subQ9])],"isStart":true}),makeQuery(id+"F28.opExtrude","CAP_FACE",FACE,{"disambiguationData":[OSD([subQ8,subQ7,sQuery(id+"F25.wireOp",EDGE,"E32"),subQ6,subQ5,subQ4])],"isStart":true})]}),makeQuery(id+"F39.opExtrude","CAP_FACE",FACE,{"disambiguationData":[OSD([subQ3])],"isStart":true})]});Q1=makeQuery(id+"F42.imprint","IMPRINT",FACE,{"disambiguationData":[TD([[makeQuery(id+"F42.imprint","IMPRINT",EDGE,{"derivedFrom":makeQuery(id+"F41.boolean.opBoolean","INTERSECT",EDGE,{"derivedFrom":[subQ14,makeQuery(id+"F41.opExtrude","CAP_FACE",FACE,{"disambiguationData":[OSD([subQ1])],"isStart":false})]})}),1.0]])]});}
            var Q2;
            Q2=makeQuery(id+"F42.imprint","IMPRINT",FACE,{"disambiguationData":[TD([[makeQuery(id+"F42.imprint","IMPRINT",EDGE,{"derivedFrom":sQuery(id+"F42.wireOp",EDGE,"E58.top")}),1.0]])]});
            var Q3;
            Q3=makeQuery(id+"F42.imprint","IMPRINT",FACE,{"disambiguationData":[TD([[makeQuery(id+"F42.imprint","IMPRINT",EDGE,{"derivedFrom":sQuery(id+"F42.wireOp",EDGE,"E57.top")}),-1.0]])]});
            extrude(context, id + "F43", {"entities" : qUnion([Q0, Q1, Q2, Q3]), "operationType" : NewBodyOperationType.REMOVE, "oppositeDirection" : true, "depth" : 25.4 * mm});
        }
        {
            var Q0;
            Q0=makeQuery(id+"F26.opExtrude","SWEPT_BODY",BODY,{"disambiguationData":[OSD([sQuery(id+"F25.wireOp",EDGE,"E33"),sQuery(id+"F25.wireOp",EDGE,"E41")])]});
            var Q1;
            Q1=makeQuery(id+"F27.opExtrude","CAP_EDGE",EDGE,{"disambiguationData":[OSD([sQuery(id+"F25.wireOp",EDGE,"E29.right")])],"isStart":false});
            transform(context, id + "F44", {"entities" : qUnion([Q0]), "transformType" : TransformType.ROTATION, "transformAxis" : qUnion([Q1]), "angle" : 180 * degree, "makeCopy" : false});
        }
        {
            var Q0;
            Q0=makeQuery(id+"F3.opExtrude","SWEPT_FACE",FACE,{"disambiguationData":[OSD([sQuery(id+"F2.wireOp",EDGE,"E4.top")])]});
            var sketch = newSketch(context, id + "F45", { "sketchPlane" : qUnion([Q0])});
            skLineSegment(sketch, "E59", {"start": v(-350.85, 118.78) * mm, "end": v(-350.85, 303.78) * mm});
            skLineSegment(sketch, "E60", {"start": v(-350.85, 303.78) * mm, "end": v(-322.93, 303.78) * mm});
            skLineSegment(sketch, "E61", {"start": v(-322.93, 303.78) * mm, "end": v(-322.93, 431.18) * mm});
            skLineSegment(sketch, "E62", {"start": v(-322.93, 431.18) * mm, "end": v(-291.51, 431.18) * mm});
            skLineSegment(sketch, "E63", {"start": v(-291.51, 431.18) * mm, "end": v(-291.51, 464.12) * mm});
            skLineSegment(sketch, "E64", {"start": v(-291.51, 464.12) * mm, "end": v(-92.84, 464.12) * mm});
            skLineSegment(sketch, "E65", {"start": v(-92.84, 464.12) * mm, "end": v(-92.84, 431.18) * mm});
            skLineSegment(sketch, "E66", {"start": v(-92.84, 431.18) * mm, "end": v(125.34, 431.18) * mm});
            skLineSegment(sketch, "E67", {"start": v(125.34, 431.18) * mm, "end": v(125.34, 488.9) * mm});
            skLineSegment(sketch, "E68", {"start": v(125.34, 488.9) * mm, "end": v(153.08, 488.9) * mm});
            skLineSegment(sketch, "E69", {"start": v(153.08, 488.9) * mm, "end": v(153.08, 49.17) * mm});
            skLineSegment(sketch, "E70", {"start": v(153.08, 49.17) * mm, "end": v(125.34, 49.17) * mm});
            skLineSegment(sketch, "E71", {"start": v(125.34, 49.17) * mm, "end": v(125.34, 106.88) * mm});
            skLineSegment(sketch, "E72", {"start": v(125.34, 106.88) * mm, "end": v(-350.85, 106.88) * mm});
            skLineSegment(sketch, "E73", {"start": v(-350.85, 106.88) * mm, "end": v(-350.85, 118.78) * mm});
            skCircle(sketch, "E74", {"center": v(0, 260.9) * mm, "radius": 101.6 * mm});
            skSolve(sketch);
        }
        {
            var Q0;
            {var subQ3=sQuery(id+"F45.wireOp",EDGE,"E65");Q0=makeQuery(id+"F45.imprint","IMPRINT",FACE,{"disambiguationData":[TD([[makeQuery(id+"F45.imprint","IMPRINT",EDGE,{"derivedFrom":subQ3}),1.0]])]});}
            cPlane(context, id + "F46", {"entities" : qUnion([Q0]), "cplaneType" : CPlaneType.OFFSET, "offset" : 22.22 * mm, "width" : 152.4 * mm, "height" : 152.4 * mm});
        }
        {
            var Q0;
            Q0=qCreatedBy(id+"F46.planeOp",FACE);
            var sketch = newSketch(context, id + "F47", { "sketchPlane" : qUnion([Q0])});
            skLineSegment(sketch, "E75.0", {"start": v(125.34, 488.9) * mm, "end": v(153.08, 488.9) * mm});
            skLineSegment(sketch, "E75.1", {"start": v(-92.84, 431.18) * mm, "end": v(125.34, 431.18) * mm});
            skLineSegment(sketch, "E75.2", {"start": v(153.08, 488.9) * mm, "end": v(153.08, 49.17) * mm});
            skLineSegment(sketch, "E75.3", {"start": v(-322.93, 431.18) * mm, "end": v(-291.51, 431.18) * mm});
            skLineSegment(sketch, "E75.4", {"start": v(-291.51, 431.18) * mm, "end": v(-291.51, 464.12) * mm});
            skLineSegment(sketch, "E75.5", {"start": v(-350.85, 303.78) * mm, "end": v(-322.93, 303.78) * mm});
            skLineSegment(sketch, "E75.6", {"start": v(125.34, 431.18) * mm, "end": v(125.34, 488.9) * mm});
            skLineSegment(sketch, "E75.7", {"start": v(-350.85, 118.78) * mm, "end": v(-350.85, 303.78) * mm});
            skLineSegment(sketch, "E75.8", {"start": v(-322.93, 303.78) * mm, "end": v(-322.93, 431.18) * mm});
            skLineSegment(sketch, "E75.9", {"start": v(153.08, 49.17) * mm, "end": v(125.34, 49.17) * mm});
            skLineSegment(sketch, "E75.10", {"start": v(125.34, 49.17) * mm, "end": v(125.34, 106.88) * mm});
            skLineSegment(sketch, "E75.11", {"start": v(-92.84, 464.12) * mm, "end": v(-92.84, 431.18) * mm});
            skLineSegment(sketch, "E75.12", {"start": v(-291.51, 464.12) * mm, "end": v(-92.84, 464.12) * mm});
            skLineSegment(sketch, "E75.13", {"start": v(125.34, 106.88) * mm, "end": v(-350.85, 106.88) * mm});
            skLineSegment(sketch, "E75.14", {"start": v(-350.85, 106.88) * mm, "end": v(-350.85, 118.78) * mm});
            skSolve(sketch);
        }
        {
            var Q0;
            Q0=makeQuery(id+"F45.imprint","IMPRINT",FACE,{"disambiguationData":[TD([[makeQuery(id+"F45.imprint","IMPRINT",EDGE,{"derivedFrom":sQuery(id+"F45.wireOp",EDGE,"E74")}),1.0]])]});
            extrude(context, id + "F48", {"entities" : qUnion([Q0]), "operationType" : NewBodyOperationType.ADD, "depth" : 22.22 * mm});
        }
        {
            var Q0;
            Q0=makeQuery(id+"F47.imprint","IMPRINT",FACE,{"disambiguationData":[TD([[makeQuery(id+"F47.imprint","IMPRINT",EDGE,{"derivedFrom":sQuery(id+"F47.wireOp",EDGE,"E75.2")}),-1.0]])]});
            extrude(context, id + "F49", {"entities" : qUnion([Q0]), "operationType" : NewBodyOperationType.ADD, "depth" : 219.07 * mm});
        }
    });
